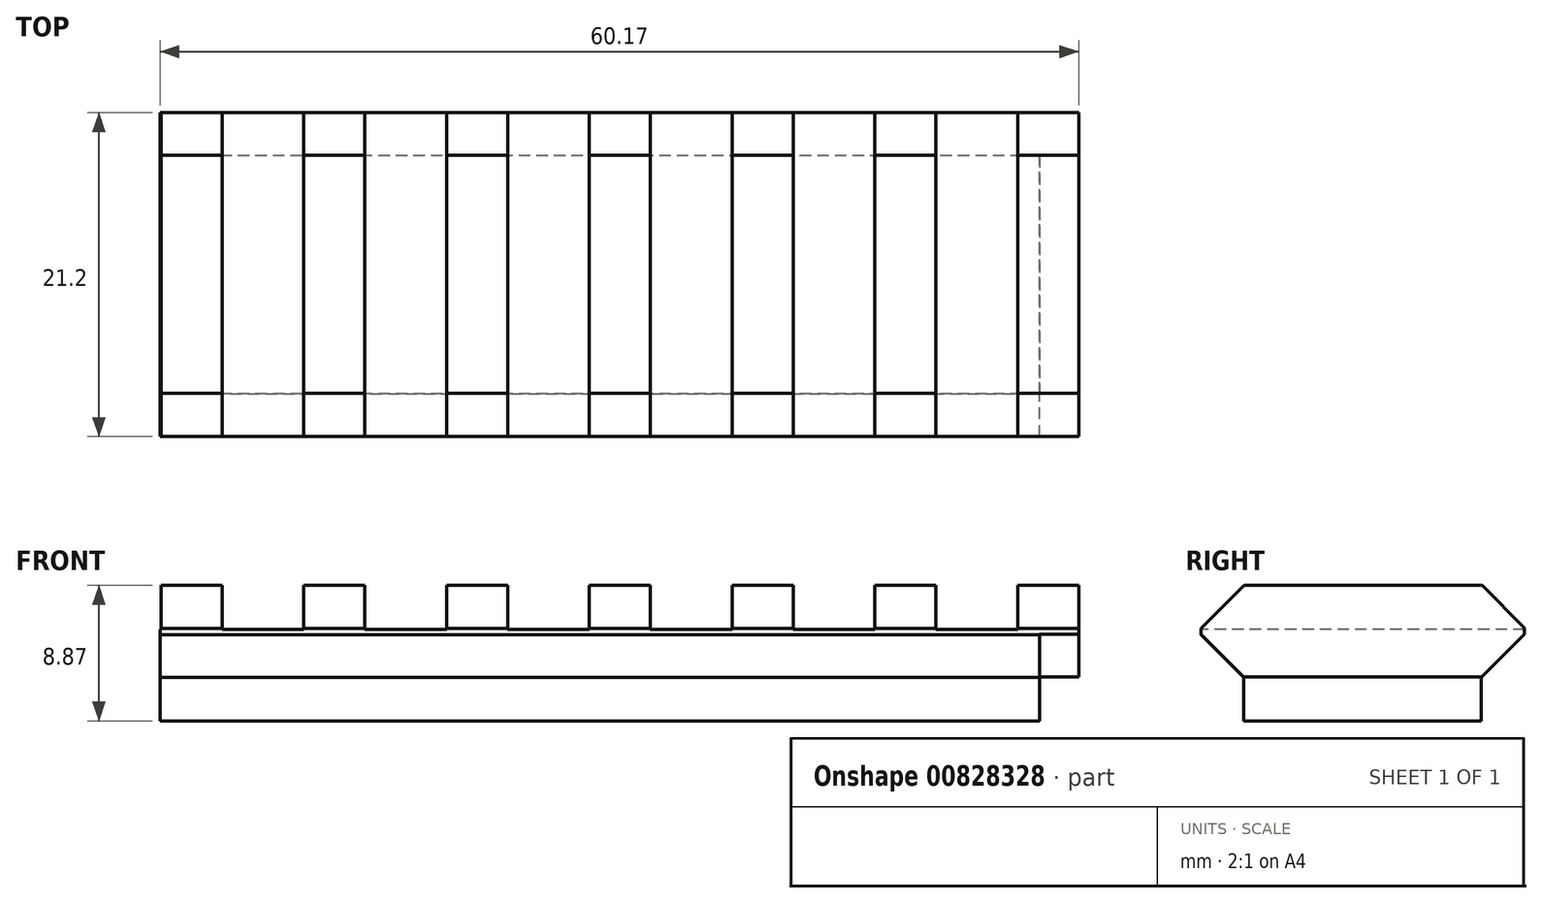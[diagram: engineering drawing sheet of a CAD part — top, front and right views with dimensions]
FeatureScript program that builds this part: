
annotation { "Feature Type Name" : "Feature", "Feature Type Description" : "" }
export const myFeature = defineFeature(function(context is Context, id is Id, definition is map)
    precondition{}
    {
        {
            var Q0;
            Q0=qCreatedBy(makeId("Front.planeOp"),FACE);
            var sketch = newSketch(context, id + "F0", { "sketchPlane" : qUnion([Q0])});
            skLineSegment(sketch, "E0", {"start": v(-14.38, 4.19) * mm, "end": v(-9.03, 4.19) * mm});
            skLineSegment(sketch, "E1", {"start": v(-9.03, 4.19) * mm, "end": v(-9.03, 10.19) * mm});
            skLineSegment(sketch, "E2", {"start": v(-9.03, 10.19) * mm, "end": v(-5.03, 10.19) * mm});
            skLineSegment(sketch, "E3", {"start": v(-5.03, 10.19) * mm, "end": v(-5.03, 4.19) * mm});
            skLineSegment(sketch, "E4", {"start": v(-5.03, 4.19) * mm, "end": v(0.32, 4.19) * mm});
            skLineSegment(sketch, "E5", {"start": v(0.32, 4.19) * mm, "end": v(0.32, 10.19) * mm});
            skLineSegment(sketch, "E6", {"start": v(0.32, 10.19) * mm, "end": v(4.32, 10.19) * mm});
            skLineSegment(sketch, "E7", {"start": v(4.32, 10.19) * mm, "end": v(4.32, 4.19) * mm});
            skPoint(sketch, "E7.endSnap0", {"position": v(-2.36, 4.19) * mm});
            skLineSegment(sketch, "E8", {"start": v(4.32, 4.19) * mm, "end": v(9.67, 4.19) * mm});
            skLineSegment(sketch, "E9", {"start": v(9.67, 4.19) * mm, "end": v(9.67, 10.19) * mm});
            skLineSegment(sketch, "E10", {"start": v(9.67, 10.19) * mm, "end": v(13.67, 10.19) * mm});
            skLineSegment(sketch, "E11", {"start": v(13.67, 10.19) * mm, "end": v(13.67, 4.19) * mm});
            skLineSegment(sketch, "E12", {"start": v(13.67, 4.19) * mm, "end": v(19.02, 4.19) * mm});
            skLineSegment(sketch, "E13", {"start": v(19.02, 4.19) * mm, "end": v(19.02, 10.19) * mm});
            skLineSegment(sketch, "E14", {"start": v(19.02, 10.19) * mm, "end": v(23.02, 10.19) * mm});
            skLineSegment(sketch, "E15", {"start": v(23.02, 10.19) * mm, "end": v(23.02, 4.19) * mm});
            skLineSegment(sketch, "E16", {"start": v(23.02, 4.19) * mm, "end": v(28.37, 4.19) * mm});
            skLineSegment(sketch, "E17", {"start": v(-21.75, 4.19) * mm, "end": v(28.37, 4.19) * mm});
            skLineSegment(sketch, "E18", {"start": v(-14.38, 4.19) * mm, "end": v(-14.38, 10.19) * mm});
            skLineSegment(sketch, "E19", {"start": v(-14.38, 10.19) * mm, "end": v(-18.38, 10.19) * mm});
            skLineSegment(sketch, "E20", {"start": v(-18.38, 10.19) * mm, "end": v(-18.38, 4.19) * mm});
            skLineSegment(sketch, "E21", {"start": v(-18.38, 4.19) * mm, "end": v(-23.73, 4.19) * mm});
            skLineSegment(sketch, "E22", {"start": v(-23.73, 4.19) * mm, "end": v(-23.73, 10.19) * mm});
            skLineSegment(sketch, "E23", {"start": v(-23.73, 10.19) * mm, "end": v(-27.73, 10.19) * mm});
            skLineSegment(sketch, "E24", {"start": v(-27.73, 10.19) * mm, "end": v(-27.73, 4.19) * mm});
            skLineSegment(sketch, "E25", {"start": v(-27.73, 4.19) * mm, "end": v(-23.73, 4.19) * mm});
            skLineSegment(sketch, "E26", {"start": v(28.37, 10.19) * mm, "end": v(28.37, 4.19) * mm});
            skLineSegment(sketch, "E27", {"start": v(28.37, 10.19) * mm, "end": v(32.37, 10.19) * mm});
            skLineSegment(sketch, "E28", {"start": v(32.37, 10.19) * mm, "end": v(32.37, 4.19) * mm});
            skLineSegment(sketch, "E29", {"start": v(32.37, 4.19) * mm, "end": v(28.37, 4.19) * mm});
            skSolve(sketch);
        }
        {
            var Q0;
            Q0 = qSketchRegion(id + "F0", true);
            extrude(context, id + "F1", {"entities" : qUnion([Q0]), "endBound" : BoundingType.SYMMETRIC, "depth" : 21.2 * mm, "offsetDistance" : 25 * mm});
        }
        {
            var Q0;
            Q0=qCreatedBy(makeId("Front.planeOp"),FACE);
            var sketch = newSketch(context, id + "F2", { "sketchPlane" : qUnion([Q0])});
            skLineSegment(sketch, "E30", {"start": v(-21.76, 4.17) * mm, "end": v(-21.76, 3.48) * mm});
            skLineSegment(sketch, "E31", {"start": v(-21.76, 3.48) * mm, "end": v(29.26, 3.48) * mm});
            skLineSegment(sketch, "E32", {"start": v(29.26, 3.48) * mm, "end": v(29.26, 4.19) * mm});
            skLineSegment(sketch, "E33", {"start": v(29.26, 4.19) * mm, "end": v(-21.76, 4.17) * mm});
            skSolve(sketch);
        }
        {
            var Q0;
            Q0=makeQuery(id+"F2.imprint","IMPRINT",FACE,{"disambiguationData":[TD([[makeQuery(id+"F2.imprint","IMPRINT",EDGE,{"derivedFrom":sQuery(id+"F2.wireOp",EDGE,"E30")}),1.0]])]});
            extrude(context, id + "F3", {"entities" : qUnion([Q0]), "operationType" : NewBodyOperationType.ADD, "endBound" : BoundingType.SYMMETRIC, "depth" : 15.6 * mm, "offsetDistance" : 25 * mm});
        }
        {
            var Q0;
            Q0=qCreatedBy(makeId("Right.planeOp"),FACE);
            var sketch = newSketch(context, id + "F4", { "sketchPlane" : qUnion([Q0])});
            skLineSegment(sketch, "E34", {"start": v(0, 0) * mm, "end": v(0, 10.3) * mm, "construction": true});
            skLineSegment(sketch, "E35", {"start": v(-6.98, 10.18) * mm, "end": v(-10.6, 10.18) * mm});
            skLineSegment(sketch, "E36", {"start": v(-10.6, 10.18) * mm, "end": v(-10.6, 4.18) * mm});
            skLineSegment(sketch, "E37", {"start": v(-10.6, 4.18) * mm, "end": v(-7.8, 4.18) * mm});
            skLineSegment(sketch, "E38", {"start": v(-7.8, 4.18) * mm, "end": v(-10.6, 6.98) * mm});
            skLineSegment(sketch, "E39", {"start": v(-13.01, 10.3) * mm, "end": v(-13.01, 0.26) * mm, "construction": true});
            skLineSegment(sketch, "E40", {"start": v(-0.88, 7.2) * mm, "end": v(1.7, 7.2) * mm, "construction": true});
            skLineSegment(sketch, "E41", {"start": v(0, 8.76) * mm, "end": v(-9.5, 8.76) * mm, "construction": true});
            skLineSegment(sketch, "E42", {"start": v(-9.5, 8.76) * mm, "end": v(-9.5, 6.02) * mm, "construction": true});
            skLineSegment(sketch, "E43", {"start": v(-9.5, 6.02) * mm, "end": v(0, 6.02) * mm, "construction": true});
            skLineSegment(sketch, "E44", {"start": v(0, 6.02) * mm, "end": v(0, 8.76) * mm});
            skLineSegment(sketch, "E45", {"start": v(-10.6, 10.18) * mm, "end": v(-11.6, 10.18) * mm});
            skLineSegment(sketch, "E46", {"start": v(-10.6, 10.18) * mm, "end": v(-10.6, 7.38) * mm});
            skLineSegment(sketch, "E47", {"start": v(-10.6, 7.38) * mm, "end": v(-7.8, 10.18) * mm});
            skLineSegment(sketch, "E48", {"start": v(-7.55, 4.16) * mm, "end": v(10.6, 4.16) * mm});
            skLineSegment(sketch, "E49", {"start": v(10.6, 4.16) * mm, "end": v(10.6, 10.2) * mm});
            skLineSegment(sketch, "E50", {"start": v(10.6, 10.2) * mm, "end": v(7.8, 10.2) * mm});
            skLineSegment(sketch, "E51", {"start": v(7.8, 10.2) * mm, "end": v(10.6, 7.4) * mm});
            skLineSegment(sketch, "E52", {"start": v(10.6, 4.16) * mm, "end": v(10.6, 6.96) * mm});
            skLineSegment(sketch, "E53", {"start": v(10.6, 6.96) * mm, "end": v(7.8, 4.16) * mm});
            skSolve(sketch);
        }
        {
            var Q0;
            Q0 = qSketchRegion(id + "F4", true);
            var Q1;
            Q1=sQuery(id+"F4.wireOp",EDGE,"E42");
            extrude(context, id + "F5", {"entities" : qUnion([Q0]), "operationType" : NewBodyOperationType.REMOVE, "surfaceEntities" : qUnion([Q1]), "endBound" : BoundingType.THROUGH_ALL, "depth" : 25 * mm, "offsetDistance" : 25 * mm, "hasSecondDirection" : true, "secondDirectionOppositeDirection" : true, "secondDirectionDepth" : 100 * mm});
        }
        {
            var Q0;
            Q0=qCreatedBy(makeId("Front.planeOp"),FACE);
            var sketch = newSketch(context, id + "F6", { "sketchPlane" : qUnion([Q0])});
            skLineSegment(sketch, "E54", {"start": v(-27.8, 7.3) * mm, "end": v(29.8, 7.3) * mm});
            skLineSegment(sketch, "E55", {"start": v(29.8, 7.3) * mm, "end": v(29.8, 1.32) * mm});
            skLineSegment(sketch, "E56", {"start": v(29.8, 1.32) * mm, "end": v(-27.8, 1.32) * mm});
            skLineSegment(sketch, "E57", {"start": v(-27.8, 1.32) * mm, "end": v(-27.8, 7.3) * mm});
            skSolve(sketch);
        }
        {
            var Q0;
            Q0 = qSketchRegion(id + "F6", true);
            extrude(context, id + "F7", {"entities" : qUnion([Q0]), "operationType" : NewBodyOperationType.ADD, "endBound" : BoundingType.SYMMETRIC, "oppositeDirection" : true, "depth" : 21.2 * mm, "offsetDistance" : 25 * mm});
        }
        {
            var Q0;
            Q0=qCreatedBy(makeId("Right.planeOp"),FACE);
            var sketch = newSketch(context, id + "F8", { "sketchPlane" : qUnion([Q0])});
            skLineSegment(sketch, "E58", {"start": v(-6.97, 10.19) * mm, "end": v(-10.6, 10.19) * mm});
            skLineSegment(sketch, "E59", {"start": v(-10.6, 10.19) * mm, "end": v(-10.6, 4.17) * mm});
            skLineSegment(sketch, "E60", {"start": v(-10.6, 4.17) * mm, "end": v(-7.8, 4.17) * mm});
            skLineSegment(sketch, "E61", {"start": v(-7.8, 4.17) * mm, "end": v(-10.6, 6.97) * mm});
            skLineSegment(sketch, "E62", {"start": v(-10.6, 10.19) * mm, "end": v(-11.6, 10.19) * mm});
            skLineSegment(sketch, "E63", {"start": v(-13.41, 4.55) * mm, "end": v(-7.77, 10.19) * mm});
            skLineSegment(sketch, "E64", {"start": v(6.97, 4.17) * mm, "end": v(10.6, 4.17) * mm});
            skLineSegment(sketch, "E65", {"start": v(10.6, 4.17) * mm, "end": v(10.6, 10.2) * mm});
            skLineSegment(sketch, "E66", {"start": v(10.6, 10.2) * mm, "end": v(7.8, 10.2) * mm});
            skLineSegment(sketch, "E67", {"start": v(7.8, 10.2) * mm, "end": v(10.6, 7.4) * mm});
            skLineSegment(sketch, "E68", {"start": v(10.6, 4.17) * mm, "end": v(11.6, 4.17) * mm});
            skLineSegment(sketch, "E69", {"start": v(13.41, 9.8) * mm, "end": v(7.77, 4.17) * mm});
            skSolve(sketch);
        }
        {
            var Q0;
            Q0 = qSketchRegion(id + "F8", true);
            extrude(context, id + "F9", {"entities" : qUnion([Q0]), "operationType" : NewBodyOperationType.REMOVE, "endBound" : BoundingType.THROUGH_ALL, "oppositeDirection" : true, "depth" : 25 * mm, "offsetDistance" : 25 * mm, "hasSecondDirection" : true, "secondDirectionOppositeDirection" : false, "secondDirectionDepth" : 50 * mm});
        }
        {
            var Q0;
            Q0=qCreatedBy(makeId("Right.planeOp"),FACE);
            var sketch = newSketch(context, id + "F10", { "sketchPlane" : qUnion([Q0])});
            skLineSegment(sketch, "E70", {"start": v(-7.8, 4.17) * mm, "end": v(-7.8, 1.17) * mm});
            skLineSegment(sketch, "E71", {"start": v(-7.8, 1.17) * mm, "end": v(-11, 1.17) * mm});
            skLineSegment(sketch, "E72", {"start": v(-11, 1.17) * mm, "end": v(-11, 4.36) * mm});
            skLineSegment(sketch, "E73", {"start": v(-11, 4.36) * mm, "end": v(-7.8, 4.17) * mm});
            skLineSegment(sketch, "E74", {"start": v(7.77, 1.17) * mm, "end": v(7.77, 4.17) * mm});
            skLineSegment(sketch, "E75", {"start": v(7.77, 4.17) * mm, "end": v(10.97, 4.17) * mm});
            skLineSegment(sketch, "E76", {"start": v(10.97, 4.17) * mm, "end": v(10.97, 0.97) * mm});
            skLineSegment(sketch, "E77", {"start": v(10.97, 0.97) * mm, "end": v(7.77, 1.17) * mm});
            skSolve(sketch);
        }
        {
            var Q0;
            Q0 = qSketchRegion(id + "F10", true);
            var Q1;
            Q1=sQuery(id+"F10.wireOp",EDGE,"E74");
            extrude(context, id + "F11", {"entities" : qUnion([Q0]), "operationType" : NewBodyOperationType.REMOVE, "surfaceEntities" : qUnion([Q1]), "endBound" : BoundingType.THROUGH_ALL, "oppositeDirection" : true, "depth" : 25 * mm, "offsetDistance" : 25 * mm, "hasSecondDirection" : true, "secondDirectionOppositeDirection" : false, "secondDirectionDepth" : 60 * mm});
        }
    });
